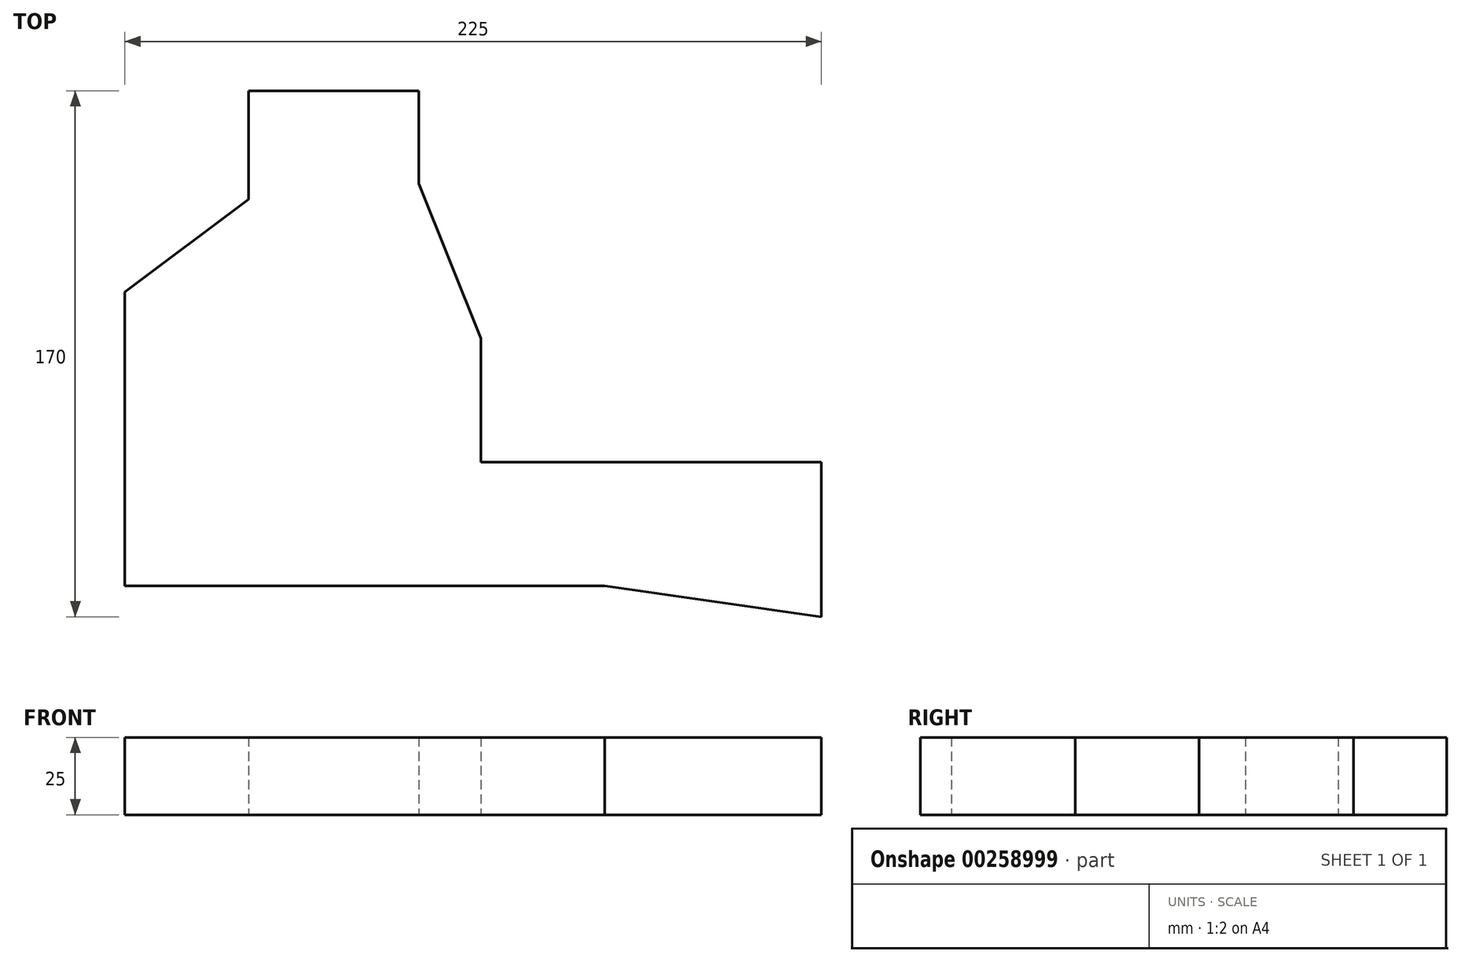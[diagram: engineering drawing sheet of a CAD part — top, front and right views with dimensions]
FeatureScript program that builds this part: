
annotation { "Feature Type Name" : "Feature", "Feature Type Description" : "" }
export const myFeature = defineFeature(function(context is Context, id is Id, definition is map)
    precondition{}
    {
        {
            var Q0;
            Q0=qCreatedBy(makeId("Top.planeOp"),FACE);
            var sketch = newSketch(context, id + "F0", { "sketchPlane" : qUnion([Q0])});
            skLineSegment(sketch, "E0", {"start": v(-108.15, 30.68) * mm, "end": v(-108.15, -64.32) * mm});
            skLineSegment(sketch, "E1", {"start": v(-108.15, -64.32) * mm, "end": v(46.85, -64.32) * mm});
            skLineSegment(sketch, "E2", {"start": v(46.85, -64.32) * mm, "end": v(116.85, -74.32) * mm});
            skLineSegment(sketch, "E3", {"start": v(116.85, -74.32) * mm, "end": v(116.85, -24.32) * mm});
            skLineSegment(sketch, "E4", {"start": v(116.85, -24.32) * mm, "end": v(6.85, -24.32) * mm});
            skLineSegment(sketch, "E5", {"start": v(6.85, -24.32) * mm, "end": v(6.85, 15.68) * mm});
            skLineSegment(sketch, "E6", {"start": v(6.85, 15.68) * mm, "end": v(-13.15, 65.68) * mm});
            skLineSegment(sketch, "E7", {"start": v(-13.15, 65.68) * mm, "end": v(-13.15, 95.68) * mm});
            skLineSegment(sketch, "E8", {"start": v(-13.15, 95.68) * mm, "end": v(-68.15, 95.68) * mm});
            skLineSegment(sketch, "E9", {"start": v(-68.15, 95.68) * mm, "end": v(-68.15, 60.68) * mm});
            skLineSegment(sketch, "E10", {"start": v(-68.15, 60.68) * mm, "end": v(-108.15, 30.68) * mm});
            skSolve(sketch);
        }
        {
            var Q0;
            Q0 = qSketchRegion(id + "F0", true);
            extrude(context, id + "F1", {"entities" : qUnion([Q0]), "depth" : 25 * mm});
        }
    });
